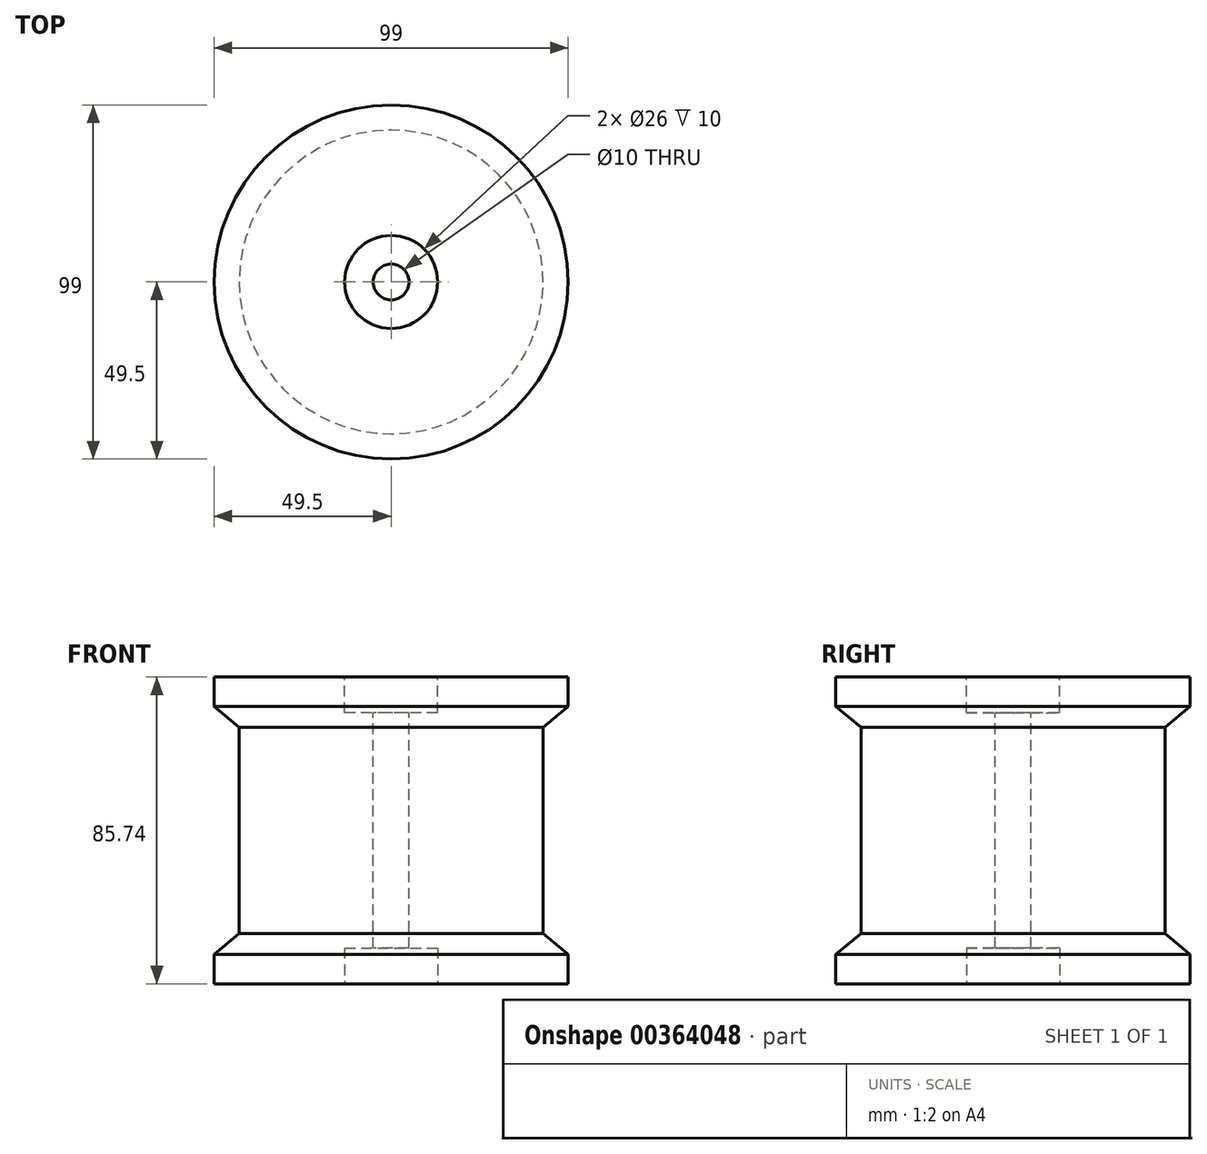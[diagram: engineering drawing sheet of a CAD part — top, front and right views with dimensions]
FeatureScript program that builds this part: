
annotation { "Feature Type Name" : "Feature", "Feature Type Description" : "" }
export const myFeature = defineFeature(function(context is Context, id is Id, definition is map)
    precondition{}
    {
        {
            var Q0;
            Q0=qCreatedBy(makeId("Front.planeOp"),FACE);
            var sketch = newSketch(context, id + "F0", { "sketchPlane" : qUnion([Q0])});
            skLineSegment(sketch, "E0", {"start": v(0, 42.87) * mm, "end": v(-49.5, 42.87) * mm});
            skLineSegment(sketch, "E1", {"start": v(-49.5, 42.87) * mm, "end": v(-49.5, 34.69) * mm});
            skLineSegment(sketch, "E2", {"start": v(-49.5, 34.69) * mm, "end": v(-42.48, 28.84) * mm});
            skLineSegment(sketch, "E3", {"start": v(-42.48, 28.84) * mm, "end": v(-42.48, 0) * mm});
            skLineSegment(sketch, "E4", {"start": v(0, 42.87) * mm, "end": v(0, 0) * mm});
            skLineSegment(sketch, "E5.MirrorCS", {"start": v(-49.5, -34.69) * mm, "end": v(-42.48, -28.84) * mm});
            skLineSegment(sketch, "E6.MirrorCS", {"start": v(-49.5, -42.87) * mm, "end": v(-49.5, -34.69) * mm});
            skLineSegment(sketch, "E7.MirrorCS", {"start": v(0, -42.87) * mm, "end": v(-49.5, -42.87) * mm});
            skLineSegment(sketch, "E8.MirrorCS", {"start": v(0, -42.87) * mm, "end": v(0, 0) * mm});
            skLineSegment(sketch, "E9.MirrorCS", {"start": v(-42.48, -28.84) * mm, "end": v(-42.48, 0) * mm});
            skSolve(sketch);
        }
        {
            var Q0;
            Q0=makeQuery(id+"F0.imprint","IMPRINT",FACE,{"disambiguationData":[TD([[makeQuery(id+"F0.imprint","IMPRINT",EDGE,{"derivedFrom":sQuery(id+"F0.wireOp",EDGE,"E0")}),1.0]])]});
            var Q1;
            Q1=sQuery(id+"F0.wireOp",EDGE,"E4");
            revolve(context, id + "F1", {"entities" : qUnion([Q0]), "axis" : qUnion([Q1]), "revolveType" : RevolveType.FULL});
        }
        {
            var Q0;
            Q0=makeQuery(id+"F1.opRevolve","SWEPT_FACE",FACE,{"disambiguationData":[OSD([sQuery(id+"F0.wireOp",EDGE,"E0")])]});
            var sketch = newSketch(context, id + "F2", { "sketchPlane" : qUnion([Q0])});
            skCircle(sketch, "E10", {"center": v(0, 0) * mm, "radius": 5 * mm});
            skCircle(sketch, "E11", {"center": v(0, 0) * mm, "radius": 13 * mm});
            skSolve(sketch);
        }
        {
            var Q0;
            Q0=makeQuery(id+"F2.imprint","IMPRINT",FACE,{"disambiguationData":[TD([[makeQuery(id+"F2.imprint","IMPRINT",EDGE,{"derivedFrom":sQuery(id+"F2.wireOp",EDGE,"E10")}),1.0]])]});
            extrude(context, id + "F3", {"entities" : qUnion([Q0]), "operationType" : NewBodyOperationType.REMOVE, "oppositeDirection" : true, "depth" : 1000 * mm});
        }
        {
            var Q0;
            Q0=makeQuery(id+"F2.imprint","IMPRINT",FACE,{"disambiguationData":[TD([[makeQuery(id+"F2.imprint","IMPRINT",EDGE,{"derivedFrom":sQuery(id+"F2.wireOp",EDGE,"E10")}),-1.0]])]});
            extrude(context, id + "F4", {"entities" : qUnion([Q0]), "operationType" : NewBodyOperationType.REMOVE, "oppositeDirection" : true, "depth" : 10 * mm});
        }
        {
            var Q0;
            Q0=makeQuery(id+"F1.opRevolve","SWEPT_FACE",FACE,{"disambiguationData":[OSD([sQuery(id+"F0.wireOp",EDGE,"E7.MirrorCS")])]});
            var sketch = newSketch(context, id + "F5", { "sketchPlane" : qUnion([Q0])});
            skCircle(sketch, "E12", {"center": v(0, 0) * mm, "radius": 13 * mm});
            skSolve(sketch);
        }
        {
            var Q0;
            Q0=makeQuery(id+"F5.imprint","IMPRINT",FACE,{"disambiguationData":[TD([[makeQuery(id+"F5.imprint","IMPRINT",EDGE,{"derivedFrom":sQuery(id+"F5.wireOp",EDGE,"E12")}),1.0]])]});
            extrude(context, id + "F6", {"entities" : qUnion([Q0]), "operationType" : NewBodyOperationType.REMOVE, "oppositeDirection" : true, "depth" : 10 * mm});
        }
    });
